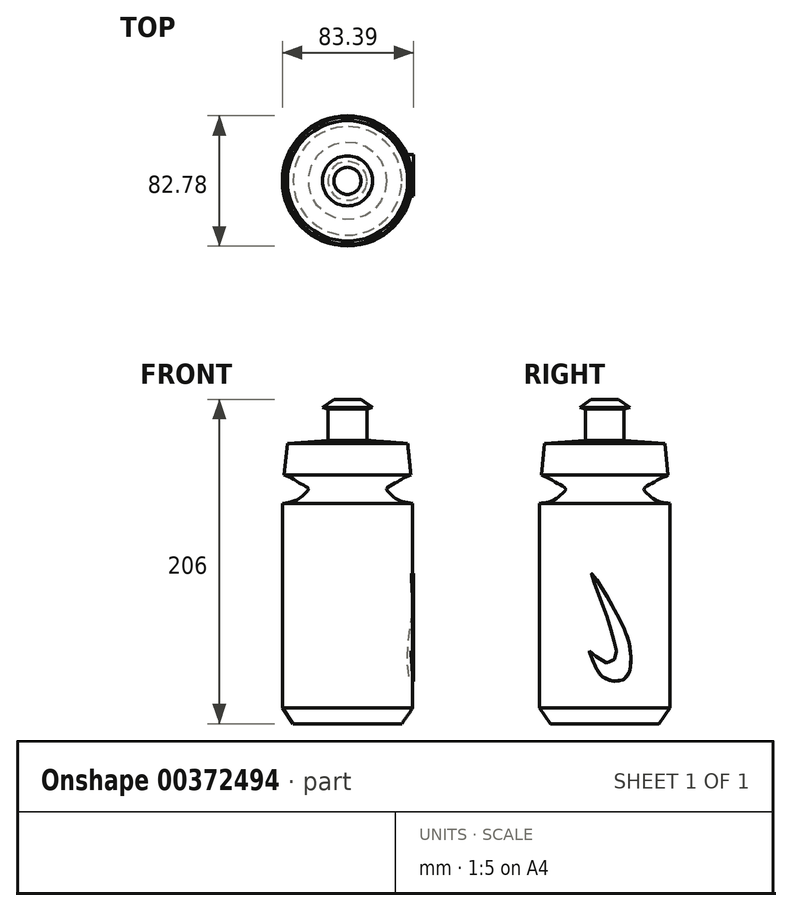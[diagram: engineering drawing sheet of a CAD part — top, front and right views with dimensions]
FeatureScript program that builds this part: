
annotation { "Feature Type Name" : "Feature", "Feature Type Description" : "" }
export const myFeature = defineFeature(function(context is Context, id is Id, definition is map)
    precondition{}
    {
        {
            var Q0;
            Q0=qCreatedBy(makeId("Top.planeOp"),FACE);
            var sketch = newSketch(context, id + "F0", { "sketchPlane" : qUnion([Q0])});
            skCircle(sketch, "E0", {"center": v(0, 0) * mm, "radius": 34.48 * mm});
            skSolve(sketch);
        }
        {
            var Q0;
            Q0=qCreatedBy(makeId("Top.planeOp"),FACE);
            cPlane(context, id + "F1", {"entities" : qUnion([Q0]), "cplaneType" : CPlaneType.OFFSET, "offset" : 10 * mm, "width" : 150 * mm, "height" : 150 * mm});
        }
        {
            var Q0;
            Q0=qCreatedBy(id+"F1.planeOp",FACE);
            var sketch = newSketch(context, id + "F2", { "sketchPlane" : qUnion([Q0])});
            skCircle(sketch, "E1", {"center": v(0, 0) * mm, "radius": 41.4 * mm});
            skSolve(sketch);
        }
        {
            var Q0;
            Q0 = qSketchRegion(id + "F0", true);
            var Q1;
            Q1 = qSketchRegion(id + "F2", true);
            loft(context, id + "F3", {"sheetProfilesArray" : [{ "sheetProfileEntities" : qUnion([Q0]) }, { "sheetProfileEntities" : qUnion([Q1]) }]});
        }
        {
            var Q0;
            Q0=makeQuery(id+"F3.opLoft","CAP_FACE",FACE,{"disambiguationData":[OSD([makeQuery(id+"F2.imprint","IMPRINT",FACE,{"disambiguationData":[TD([[makeQuery(id+"F2.imprint","IMPRINT",EDGE,{"derivedFrom":sQuery(id+"F2.wireOp",EDGE,"E1")}),1.0]])]})])],"isStart":true});
            extrude(context, id + "F4", {"entities" : qUnion([Q0]), "operationType" : NewBodyOperationType.ADD, "depth" : 130 * mm});
        }
        {
            var Q0;
            Q0=makeQuery(id+"F4.opExtrude","CAP_FACE",FACE,{"disambiguationData":[OSD([makeQuery(id+"F2.imprint","IMPRINT",FACE,{"disambiguationData":[TD([[makeQuery(id+"F2.imprint","IMPRINT",EDGE,{"derivedFrom":sQuery(id+"F2.wireOp",EDGE,"E1")}),1.0]])]})])],"isStart":false});
            cPlane(context, id + "F5", {"entities" : qUnion([Q0]), "cplaneType" : CPlaneType.OFFSET, "offset" : 3 * mm, "width" : 150 * mm, "height" : 150 * mm});
        }
        {
            var Q0;
            Q0=qCreatedBy(id+"F5.planeOp",FACE);
            var sketch = newSketch(context, id + "F6", { "sketchPlane" : qUnion([Q0])});
            skCircle(sketch, "E2", {"center": v(0, 0) * mm, "radius": 30.84 * mm});
            skSolve(sketch);
        }
        {
            var Q0;
            Q0=qCreatedBy(id+"F5.planeOp",FACE);
            cPlane(context, id + "F7", {"entities" : qUnion([Q0]), "cplaneType" : CPlaneType.OFFSET, "offset" : 3 * mm, "width" : 150 * mm, "height" : 150 * mm});
        }
        {
            var Q0;
            Q0=qCreatedBy(id+"F7.planeOp",FACE);
            var sketch = newSketch(context, id + "F8", { "sketchPlane" : qUnion([Q0])});
            skCircle(sketch, "E3", {"center": v(0, 0) * mm, "radius": 27.3 * mm});
            skSolve(sketch);
        }
        {
            var Q0;
            Q0=qCreatedBy(id+"F7.planeOp",FACE);
            cPlane(context, id + "F9", {"entities" : qUnion([Q0]), "cplaneType" : CPlaneType.OFFSET, "offset" : 3 * mm, "width" : 150 * mm, "height" : 150 * mm});
        }
        {
            var Q0;
            Q0=qCreatedBy(id+"F9.planeOp",FACE);
            var sketch = newSketch(context, id + "F10", { "sketchPlane" : qUnion([Q0])});
            skCircle(sketch, "E4", {"center": v(0, 0) * mm, "radius": 24.75 * mm});
            skSolve(sketch);
        }
        {
            var Q0;
            Q0=qCreatedBy(id+"F9.planeOp",FACE);
            cPlane(context, id + "F11", {"entities" : qUnion([Q0]), "cplaneType" : CPlaneType.OFFSET, "offset" : 3 * mm, "width" : 150 * mm, "height" : 150 * mm});
        }
        {
            var Q0;
            Q0=qCreatedBy(id+"F11.planeOp",FACE);
            var sketch = newSketch(context, id + "F12", { "sketchPlane" : qUnion([Q0])});
            skCircle(sketch, "E5", {"center": v(0, 0) * mm, "radius": 28.72 * mm});
            skSolve(sketch);
        }
        {
            var Q0;
            Q0=qCreatedBy(id+"F11.planeOp",FACE);
            cPlane(context, id + "F13", {"entities" : qUnion([Q0]), "cplaneType" : CPlaneType.OFFSET, "offset" : 3 * mm, "width" : 150 * mm, "height" : 150 * mm});
        }
        {
            var Q0;
            Q0=qCreatedBy(id+"F13.planeOp",FACE);
            var sketch = newSketch(context, id + "F14", { "sketchPlane" : qUnion([Q0])});
            skCircle(sketch, "E6", {"center": v(0, 0) * mm, "radius": 33.63 * mm});
            skSolve(sketch);
        }
        {
            var Q0;
            Q0=qCreatedBy(id+"F13.planeOp",FACE);
            cPlane(context, id + "F15", {"entities" : qUnion([Q0]), "cplaneType" : CPlaneType.OFFSET, "offset" : 3 * mm, "width" : 150 * mm, "height" : 150 * mm});
        }
        {
            var Q0;
            Q0=qCreatedBy(id+"F15.planeOp",FACE);
            var sketch = newSketch(context, id + "F16", { "sketchPlane" : qUnion([Q0])});
            skCircle(sketch, "E7", {"center": v(0, 0) * mm, "radius": 40.26 * mm});
            skSolve(sketch);
        }
        {
            var Q0;
            Q0=makeQuery(id+"F4.opExtrude","CAP_FACE",FACE,{"disambiguationData":[OSD([makeQuery(id+"F2.imprint","IMPRINT",FACE,{"disambiguationData":[TD([[makeQuery(id+"F2.imprint","IMPRINT",EDGE,{"derivedFrom":sQuery(id+"F2.wireOp",EDGE,"E1")}),1.0]])]})])],"isStart":false});
            var Q1;
            Q1 = qSketchRegion(id + "F6", true);
            var Q2;
            Q2 = qSketchRegion(id + "F8", true);
            var Q3;
            Q3 = qSketchRegion(id + "F10", true);
            var Q4;
            Q4 = qSketchRegion(id + "F12", true);
            var Q5;
            Q5 = qSketchRegion(id + "F14", true);
            var Q6;
            Q6 = qSketchRegion(id + "F16", true);
            loft(context, id + "F17", {"sheetProfilesArray" : [{ "sheetProfileEntities" : qUnion([Q0]) }, { "sheetProfileEntities" : qUnion([Q1]) }, { "sheetProfileEntities" : qUnion([Q2]) }, { "sheetProfileEntities" : qUnion([Q3]) }, { "sheetProfileEntities" : qUnion([Q4]) }, { "sheetProfileEntities" : qUnion([Q5]) }, { "sheetProfileEntities" : qUnion([Q6]) }]});
        }
        {
            var Q0;
            Q0=qCreatedBy(id+"F15.planeOp",FACE);
            cPlane(context, id + "F18", {"entities" : qUnion([Q0]), "cplaneType" : CPlaneType.OFFSET, "offset" : 20 * mm, "width" : 150 * mm, "height" : 150 * mm});
        }
        {
            var Q0;
            Q0=qCreatedBy(id+"F18.planeOp",FACE);
            var sketch = newSketch(context, id + "F19", { "sketchPlane" : qUnion([Q0])});
            skCircle(sketch, "E8", {"center": v(0, 0) * mm, "radius": 38.23 * mm});
            skSolve(sketch);
        }
        {
            var Q0;
            Q0 = qSketchRegion(id + "F16", true);
            var Q1;
            Q1 = qSketchRegion(id + "F19", true);
            loft(context, id + "F20", {"sheetProfilesArray" : [{ "sheetProfileEntities" : qUnion([Q0]) }, { "sheetProfileEntities" : qUnion([Q1]) }]});
        }
        {
            var Q0;
            Q0=qCreatedBy(id+"F18.planeOp",FACE);
            cPlane(context, id + "F21", {"entities" : qUnion([Q0]), "cplaneType" : CPlaneType.OFFSET, "offset" : 2 * mm, "width" : 150 * mm, "height" : 150 * mm});
        }
        {
            var Q0;
            Q0=qCreatedBy(id+"F21.planeOp",FACE);
            var sketch = newSketch(context, id + "F22", { "sketchPlane" : qUnion([Q0])});
            skCircle(sketch, "E9", {"center": v(0, 0) * mm, "radius": 12.31 * mm});
            skSolve(sketch);
        }
        {
            var Q1;
            Q1 = qSketchRegion(id + "F19", true);
            var Q2;
            Q2 = qSketchRegion(id + "F22", true);
            loft(context, id + "F23", {"operationType" : NewBodyOperationType.ADD, "sheetProfilesArray" : [{ "sheetProfileEntities" : qUnion([Q1]) }, { "sheetProfileEntities" : qUnion([Q2]) }]});
        }
        {
            var Q0;
            Q0=makeQuery(id+"F22.imprint","IMPRINT",FACE,{"disambiguationData":[TD([[makeQuery(id+"F22.imprint","IMPRINT",EDGE,{"derivedFrom":sQuery(id+"F22.wireOp",EDGE,"E9")}),1.0]])]});
            extrude(context, id + "F24", {"entities" : qUnion([Q0]), "operationType" : NewBodyOperationType.ADD, "depth" : 20 * mm});
        }
        {
            var Q0;
            Q0=makeQuery(id+"F24.opExtrude","CAP_FACE",FACE,{"disambiguationData":[OSD([sQuery(id+"F22.wireOp",EDGE,"E9")])],"isStart":false});
            cPlane(context, id + "F25", {"entities" : qUnion([Q0]), "cplaneType" : CPlaneType.OFFSET, "offset" : 1 * mm, "width" : 150 * mm, "height" : 150 * mm});
        }
        {
            var Q0;
            Q0=qCreatedBy(id+"F25.planeOp",FACE);
            var sketch = newSketch(context, id + "F26", { "sketchPlane" : qUnion([Q0])});
            skCircle(sketch, "E10", {"center": v(0, 0) * mm, "radius": 15.89 * mm});
            skSolve(sketch);
        }
        {
            var Q1;
            Q1=makeQuery(id+"F26.imprint","IMPRINT",FACE,{"disambiguationData":[TD([[makeQuery(id+"F26.imprint","IMPRINT",EDGE,{"derivedFrom":sQuery(id+"F26.wireOp",EDGE,"E10")}),1.0]])]});
            var Q2;
            Q2=makeQuery(id+"F24.opExtrude","CAP_FACE",FACE,{"disambiguationData":[OSD([sQuery(id+"F22.wireOp",EDGE,"E9")])],"isStart":false});
            loft(context, id + "F27", {"operationType" : NewBodyOperationType.ADD, "sheetProfilesArray" : [{ "sheetProfileEntities" : qUnion([Q1]) }, { "sheetProfileEntities" : qUnion([Q2]) }]});
        }
        {
            var Q0;
            Q0=qCreatedBy(id+"F25.planeOp",FACE);
            cPlane(context, id + "F28", {"entities" : qUnion([Q0]), "cplaneType" : CPlaneType.OFFSET, "offset" : 5 * mm, "width" : 150 * mm, "height" : 150 * mm});
        }
        {
            var Q0;
            Q0=qCreatedBy(id+"F28.planeOp",FACE);
            var sketch = newSketch(context, id + "F29", { "sketchPlane" : qUnion([Q0])});
            skCircle(sketch, "E11", {"center": v(0, 0) * mm, "radius": 8.6 * mm});
            skSolve(sketch);
        }
        {
            var Q1;
            Q1 = qSketchRegion(id + "F26", true);
            var Q2;
            Q2 = qSketchRegion(id + "F29", true);
            loft(context, id + "F30", {"operationType" : NewBodyOperationType.ADD, "sheetProfilesArray" : [{ "sheetProfileEntities" : qUnion([Q1]) }, { "sheetProfileEntities" : qUnion([Q2]) }]});
        }
        {
            var Q0;
            Q0=qCreatedBy(makeId("Right.planeOp"),FACE);
            var sketch = newSketch(context, id + "F31", { "sketchPlane" : qUnion([Q0])});
            skFitSpline(sketch, "E12", {"points": [v(-9.63, 46.4) * mm, v(0, 38.96) * mm, v(7, 42.47) * mm, v(5.7, 52.97) * mm, v(0, 71.8) * mm, v(-8.32, 95.44) * mm, v(6.57, 71.8) * mm, v(16.2, 47.28) * mm, v(13.13, 28.9) * mm, v(0, 28.9) * mm, v(-7, 38.96) * mm, v(-9.63, 46.4) * mm]});
            skSolve(sketch);
        }
        {
            var Q0;
            Q0 = qSketchRegion(id + "F31", true);
            extrude(context, id + "F32", {"entities" : qUnion([Q0]), "operationType" : NewBodyOperationType.ADD, "depth" : 42 * mm});
        }
    });
